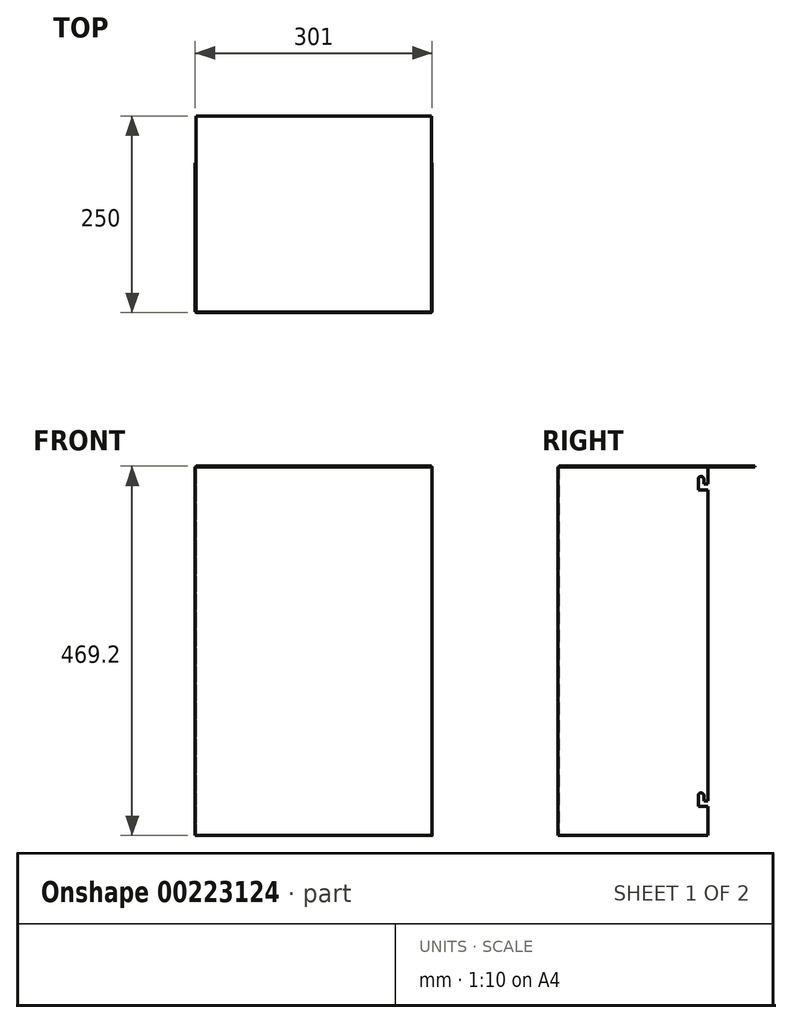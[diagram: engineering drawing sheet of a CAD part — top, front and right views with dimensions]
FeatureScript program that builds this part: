
annotation { "Feature Type Name" : "Feature", "Feature Type Description" : "" }
export const myFeature = defineFeature(function(context is Context, id is Id, definition is map)
    precondition{}
    {
        {
            var Q0;
            Q0=qCreatedBy(makeId("Top.planeOp"),FACE);
            var sketch = newSketch(context, id + "F0", { "sketchPlane" : qUnion([Q0])});
            skLineSegment(sketch, "E0", {"start": v(-2, 0) * mm, "end": v(-299, 0) * mm});
            skLineSegment(sketch, "E1", {"start": v(-301, 2) * mm, "end": v(-301, 190) * mm});
            skLineSegment(sketch, "E2", {"start": v(0, 2) * mm, "end": v(0, 190) * mm});
            skPoint(sketch, "E3.visualSharp", {"position": v(-301, 0) * mm});
            skArc(sketch, "E3.filletArc", {"start": v(-301, 2) * mm, "mid": v(-300.41, 0.59) * mm, "end": v(-299, 0) * mm});
            skPoint(sketch, "E4.visualSharp", {"position": v(0, 0) * mm});
            skArc(sketch, "E4.filletArc", {"start": v(-2, 0) * mm, "mid": v(-0.59, 0.59) * mm, "end": v(0, 2) * mm});
            skLineSegment(sketch, "E5.0", {"start": v(-299.8, 2) * mm, "end": v(-299.8, 190) * mm});
            skLineSegment(sketch, "E6.0", {"start": v(-2, 1.2) * mm, "end": v(-299, 1.2) * mm});
            skLineSegment(sketch, "E7.0", {"start": v(-1.2, 2) * mm, "end": v(-1.2, 190) * mm});
            skPoint(sketch, "E8.visualSharp", {"position": v(-1.2, 1.2) * mm});
            skArc(sketch, "E8.filletArc", {"start": v(-2, 1.2) * mm, "mid": v(-1.43, 1.43) * mm, "end": v(-1.2, 2) * mm});
            skPoint(sketch, "E9.visualSharp", {"position": v(-299.8, 1.2) * mm});
            skArc(sketch, "E9.filletArc", {"start": v(-299.8, 2) * mm, "mid": v(-299.57, 1.43) * mm, "end": v(-299, 1.2) * mm});
            skLineSegment(sketch, "E10", {"start": v(-1.2, 190) * mm, "end": v(0, 190) * mm});
            skLineSegment(sketch, "E11", {"start": v(-301, 190) * mm, "end": v(-299.8, 190) * mm});
            skSolve(sketch);
        }
        {
            var Q0;
            Q0=makeQuery(id+"F0.imprint","IMPRINT",FACE,{"disambiguationData":[TD([[makeQuery(id+"F0.imprint","IMPRINT",EDGE,{"derivedFrom":sQuery(id+"F0.wireOp",EDGE,"E0")}),-1.0]])]});
            extrude(context, id + "F1", {"entities" : qUnion([Q0]), "depth" : 468 * mm});
        }
        {
            var Q0;
            Q0=makeQuery(id+"F1.opExtrude","CAP_FACE",FACE,{"disambiguationData":[OSD([sQuery(id+"F0.wireOp",EDGE,"E0"),sQuery(id+"F0.wireOp",EDGE,"E1"),sQuery(id+"F0.wireOp",EDGE,"E2"),sQuery(id+"F0.wireOp",EDGE,"E3.filletArc"),sQuery(id+"F0.wireOp",EDGE,"E4.filletArc"),sQuery(id+"F0.wireOp",EDGE,"E5.0"),sQuery(id+"F0.wireOp",EDGE,"E6.0"),sQuery(id+"F0.wireOp",EDGE,"E7.0"),sQuery(id+"F0.wireOp",EDGE,"E8.filletArc"),sQuery(id+"F0.wireOp",EDGE,"E9.filletArc"),sQuery(id+"F0.wireOp",EDGE,"E10"),sQuery(id+"F0.wireOp",EDGE,"E11")])],"isStart":false});
            var sketch = newSketch(context, id + "F2", { "sketchPlane" : qUnion([Q0])});
            skLineSegment(sketch, "E12", {"start": v(-301, 190) * mm, "end": v(0, 190) * mm});
            skSolve(sketch);
        }
        {
            var Q0;
            {var subQ1=makeQuery(id+"F1.opExtrude","CAP_EDGE",EDGE,{"disambiguationData":[OSD([sQuery(id+"F0.wireOp",EDGE,"E5.0")])],"isStart":false});Q0=makeQuery(id+"F2.imprint","IMPRINT",FACE,{"disambiguationData":[TD([[makeQuery(id+"F2.imprint","IMPRINT",EDGE,{"derivedFrom":subQ1}),-1.0]])]});}
            extrude(context, id + "F3", {"entities" : qUnion([Q0]), "depth" : 1.2 * mm});
        }
        {
            var Q0;
            Q0=makeQuery(id+"F3.opExtrude","SWEPT_FACE",FACE,{"disambiguationData":[OSD([sQuery(id+"F2.wireOp",EDGE,"E12")])]});
            extrude(context, id + "F4", {"entities" : qUnion([Q0]), "operationType" : NewBodyOperationType.ADD, "depth" : 60 * mm});
        }
        {
            var Q0;
            Q0=makeQuery(id+"F1.opExtrude","SWEPT_FACE",FACE,{"disambiguationData":[OSD([sQuery(id+"F0.wireOp",EDGE,"E2")])]});
            var sketch = newSketch(context, id + "F5", { "sketchPlane" : qUnion([Q0])});
            skLineSegment(sketch, "E13", {"start": v(190, 439.34) * mm, "end": v(178, 439.34) * mm});
            skLineSegment(sketch, "E14", {"start": v(178, 439.34) * mm, "end": v(178, 452.84) * mm});
            skLineSegment(sketch, "E15", {"start": v(185, 452.84) * mm, "end": v(185, 446.34) * mm});
            skLineSegment(sketch, "E16", {"start": v(185, 446.34) * mm, "end": v(190, 446.34) * mm});
            skArc(sketch, "E17", {"start": v(185, 452.84) * mm, "mid": v(181.5, 456.34) * mm, "end": v(178, 452.84) * mm});
            skPoint(sketch, "E17.centerSnap0", {"position": v(181.5, 456.34) * mm});
            skPoint(sketch, "E18.orphan", {"position": v(178, 456.34) * mm});
            skPoint(sketch, "E19.orphan", {"position": v(185, 456.34) * mm});
            skLineSegment(sketch, "E20", {"start": v(190, 37.3) * mm, "end": v(178, 37.3) * mm});
            skLineSegment(sketch, "E21", {"start": v(178, 37.3) * mm, "end": v(178, 50.8) * mm});
            skLineSegment(sketch, "E22", {"start": v(190, 37.3) * mm, "end": v(190, 44.3) * mm});
            skLineSegment(sketch, "E23", {"start": v(190, 44.3) * mm, "end": v(185, 44.3) * mm});
            skLineSegment(sketch, "E24", {"start": v(185, 44.3) * mm, "end": v(185, 50.8) * mm});
            skArc(sketch, "E25", {"start": v(185, 50.8) * mm, "mid": v(181.5, 54.3) * mm, "end": v(178, 50.8) * mm});
            skSolve(sketch);
        }
        {
            var Q0;
            {var subQ1=sQuery(id+"F5.wireOp",EDGE,"E13");Q0=makeQuery(id+"F5.imprint","IMPRINT",FACE,{"disambiguationData":[TD([[makeQuery(id+"F5.imprint","IMPRINT",EDGE,{"derivedFrom":subQ1}),-1.0]])]});}
            extrude(context, id + "F6", {"entities" : qUnion([Q0]), "operationType" : NewBodyOperationType.REMOVE, "oppositeDirection" : true, "depth" : 1.2 * mm});
        }
        {
            var Q0;
            Q0 = qSketchRegion(id + "F5", true);
            extrude(context, id + "F7", {"entities" : qUnion([Q0]), "operationType" : NewBodyOperationType.REMOVE, "oppositeDirection" : true, "depth" : 1.2 * mm});
        }
        {
            var Q0;
            Q0=makeQuery(id+"F1.opExtrude","SWEPT_FACE",FACE,{"disambiguationData":[OSD([sQuery(id+"F0.wireOp",EDGE,"E5.0")])]});
            var sketch = newSketch(context, id + "F8", { "sketchPlane" : qUnion([Q0])});
            skLineSegment(sketch, "E26.0.0", {"start": v(185, 44.3) * mm, "end": v(190, 44.3) * mm});
            skLineSegment(sketch, "E26.0.1", {"start": v(190, 44.3) * mm, "end": v(190, 439.34) * mm});
            skLineSegment(sketch, "E26.0.2", {"start": v(190, 439.34) * mm, "end": v(178, 439.34) * mm});
            skLineSegment(sketch, "E26.0.3", {"start": v(178, 439.34) * mm, "end": v(178, 452.84) * mm});
            skArc(sketch, "E26.0.4", {"start": v(178, 452.84) * mm, "mid": v(181.5, 456.34) * mm, "end": v(185, 452.84) * mm});
            skLineSegment(sketch, "E26.0.5", {"start": v(185, 452.84) * mm, "end": v(185, 446.34) * mm});
            skLineSegment(sketch, "E26.0.6", {"start": v(185, 446.34) * mm, "end": v(190, 446.34) * mm});
            skLineSegment(sketch, "E26.0.7", {"start": v(190, 446.34) * mm, "end": v(190, 468) * mm});
            skLineSegment(sketch, "E26.0.8", {"start": v(190, 468) * mm, "end": v(2, 468) * mm});
            skLineSegment(sketch, "E26.0.9", {"start": v(2, 468) * mm, "end": v(2, 0) * mm});
            skLineSegment(sketch, "E26.0.10", {"start": v(2, 0) * mm, "end": v(190, 0) * mm});
            skLineSegment(sketch, "E26.0.11", {"start": v(190, 0) * mm, "end": v(190, 37.3) * mm});
            skLineSegment(sketch, "E26.0.12", {"start": v(190, 37.3) * mm, "end": v(178, 37.3) * mm});
            skLineSegment(sketch, "E26.0.13", {"start": v(178, 37.3) * mm, "end": v(178, 50.8) * mm});
            skArc(sketch, "E26.0.14", {"start": v(178, 50.8) * mm, "mid": v(181.5, 54.3) * mm, "end": v(185, 50.8) * mm});
            skLineSegment(sketch, "E26.0.15", {"start": v(185, 50.8) * mm, "end": v(185, 44.3) * mm});
            skLineSegment(sketch, "E27.0.1", {"start": v(190, 0) * mm, "end": v(190, 468) * mm});
            skSolve(sketch);
        }
        {
            var Q0;
            {var subQ0=sQuery(id+"F8.wireOp",EDGE,"E26.0.0");Q0=makeQuery(id+"F8.imprint","IMPRINT",FACE,{"disambiguationData":[TD([[makeQuery(id+"F8.imprint","IMPRINT",EDGE,{"derivedFrom":subQ0}),-1.0]])]});}
            var Q1;
            {var subQ0=sQuery(id+"F8.wireOp",EDGE,"E26.0.2");Q1=makeQuery(id+"F8.imprint","IMPRINT",FACE,{"disambiguationData":[TD([[makeQuery(id+"F8.imprint","IMPRINT",EDGE,{"derivedFrom":subQ0}),-1.0]])]});}
            extrude(context, id + "F9", {"entities" : qUnion([Q0, Q1]), "operationType" : NewBodyOperationType.REMOVE, "oppositeDirection" : true, "depth" : 1.2 * mm});
        }
    });
